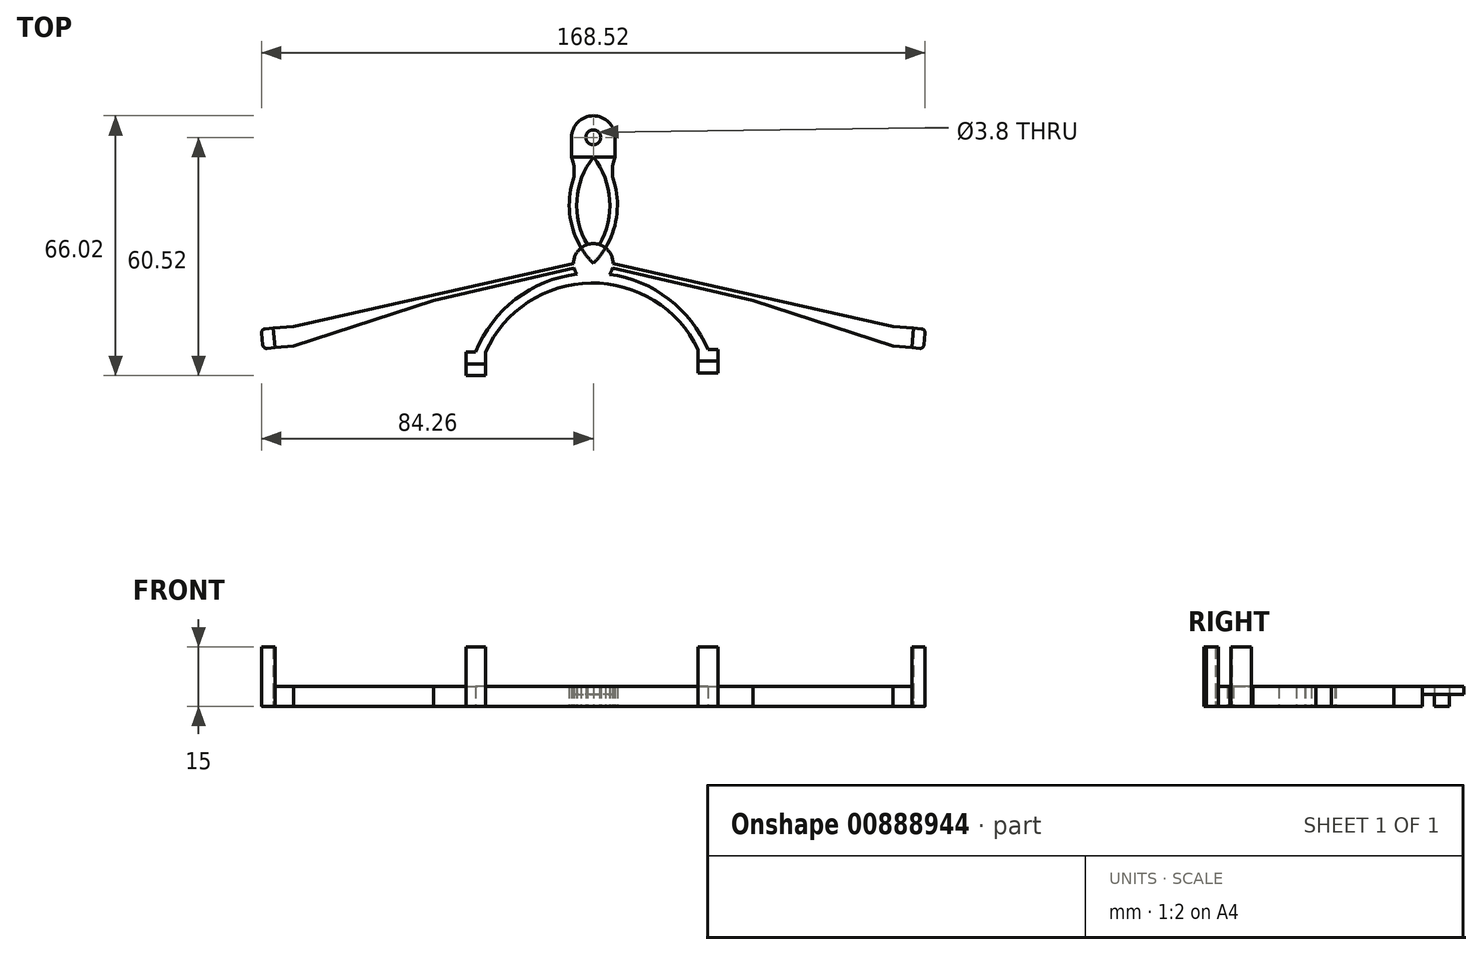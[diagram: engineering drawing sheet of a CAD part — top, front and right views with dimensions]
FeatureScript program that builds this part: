
annotation { "Feature Type Name" : "Feature", "Feature Type Description" : "" }
export const myFeature = defineFeature(function(context is Context, id is Id, definition is map)
    precondition{}
    {
        {
            var Q0;
            Q0=qCreatedBy(makeId("Top.planeOp"),FACE);
            var sketch = newSketch(context, id + "F0", { "sketchPlane" : qUnion([Q0])});
            skLineSegment(sketch, "E0.bottom", {"start": v(82.5, 27) * mm, "end": v(-82.5, 27) * mm, "construction": true});
            skLineSegment(sketch, "E0.top", {"start": v(82.5, -27) * mm, "end": v(-82.5, -27) * mm, "construction": true});
            skPoint(sketch, "E0.middle", {"position": v(0, 0) * mm});
            skPoint(sketch, "E1", {"position": v(0, 27) * mm});
            skPoint(sketch, "E2.middle", {"position": v(0, 29.5) * mm});
            skCircle(sketch, "E3", {"center": v(0, 32) * mm, "radius": 1.9 * mm});
            skLineSegment(sketch, "E4.bottom", {"start": v(-5.5, 27) * mm, "end": v(5.5, 27) * mm});
            skLineSegment(sketch, "E4.left", {"start": v(-5.5, 27) * mm, "end": v(-5.5, 32) * mm});
            skLineSegment(sketch, "E4.right", {"start": v(5.5, 27) * mm, "end": v(5.5, 32) * mm});
            skArc(sketch, "E5", {"start": v(5.5, 32) * mm, "mid": v(0, 37.5) * mm, "end": v(-5.5, 32) * mm});
            skCircle(sketch, "E6", {"center": v(0, 0) * mm, "radius": 5 * mm});
            skLineSegment(sketch, "E7", {"start": v(-82.5, 0) * mm, "end": v(82.5, 0) * mm, "construction": true});
            skArc(sketch, "E8", {"start": v(0, 29.5) * mm, "mid": v(-6.1, 14.75) * mm, "end": v(0, 0) * mm});
            skArc(sketch, "E9", {"start": v(0, 0) * mm, "mid": v(6.1, 14.75) * mm, "end": v(0, 29.5) * mm});
            skPoint(sketch, "E10", {"position": v(0, 5) * mm});
            skPoint(sketch, "E11", {"position": v(0, 2.5) * mm});
            skArc(sketch, "E12", {"start": v(0, 2.5) * mm, "mid": v(4.22, 14.75) * mm, "end": v(0, 27) * mm});
            skArc(sketch, "E13", {"start": v(0, 27) * mm, "mid": v(-4.23, 14.75) * mm, "end": v(0, 2.5) * mm});
            skLineSegment(sketch, "E14", {"start": v(-5, 0) * mm, "end": v(0, 0) * mm});
            skLineSegment(sketch, "E15", {"start": v(5, 0) * mm, "end": v(0, 0) * mm});
            skPoint(sketch, "E16", {"position": v(-2.5, 0) * mm});
            skPoint(sketch, "E17", {"position": v(2.5, 0) * mm});
            skArc(sketch, "E18", {"start": v(5.5, 27) * mm, "mid": v(4.84, 23.38) * mm, "end": v(5.5, 19.76) * mm});
            skArc(sketch, "E19", {"start": v(-5.5, 19.76) * mm, "mid": v(-4.87, 23.38) * mm, "end": v(-5.5, 27) * mm});
            skLineSegment(sketch, "E20", {"start": v(-82.5, -27) * mm, "end": v(-82.5, 27) * mm});
            skLineSegment(sketch, "E21", {"start": v(-80.9, -21.44) * mm, "end": v(-81.35, -16.46) * mm});
            skLineSegment(sketch, "E22", {"start": v(-80.9, -21.44) * mm, "end": v(-82.93, -21.62) * mm});
            skLineSegment(sketch, "E23", {"start": v(-81.35, -16.46) * mm, "end": v(-83.37, -16.64) * mm});
            skLineSegment(sketch, "E24", {"start": v(-83.98, -20.74) * mm, "end": v(-84.25, -17.7) * mm});
            skPoint(sketch, "E25.visualSharp", {"position": v(-84.34, -16.73) * mm});
            skArc(sketch, "E25.filletArc", {"start": v(-83.37, -16.64) * mm, "mid": v(-84.03, -16.99) * mm, "end": v(-84.25, -17.7) * mm});
            skPoint(sketch, "E26.visualSharp", {"position": v(-83.9, -21.71) * mm});
            skArc(sketch, "E26.filletArc", {"start": v(-83.98, -20.74) * mm, "mid": v(-83.64, -21.4) * mm, "end": v(-82.93, -21.62) * mm});
            skPoint(sketch, "E27", {"position": v(-81.13, -18.95) * mm});
            skLineSegment(sketch, "E28", {"start": v(82.5, -27) * mm, "end": v(82.5, 0) * mm});
            skLineSegment(sketch, "E29", {"start": v(-80.9, -21.44) * mm, "end": v(-80.9, -27) * mm});
            skLineSegment(sketch, "E30", {"start": v(80.9, -21.44) * mm, "end": v(81.35, -16.46) * mm});
            skLineSegment(sketch, "E31", {"start": v(81.35, -16.46) * mm, "end": v(83.37, -16.64) * mm});
            skLineSegment(sketch, "E32", {"start": v(84.25, -17.7) * mm, "end": v(83.98, -20.74) * mm});
            skLineSegment(sketch, "E33", {"start": v(82.93, -21.62) * mm, "end": v(80.9, -21.44) * mm});
            skPoint(sketch, "E34.visualSharp", {"position": v(84.34, -16.73) * mm});
            skArc(sketch, "E34.filletArc", {"start": v(84.25, -17.7) * mm, "mid": v(84.03, -16.99) * mm, "end": v(83.37, -16.64) * mm});
            skPoint(sketch, "E35.visualSharp", {"position": v(83.9, -21.71) * mm});
            skArc(sketch, "E35.filletArc", {"start": v(82.93, -21.62) * mm, "mid": v(83.64, -21.4) * mm, "end": v(83.98, -20.74) * mm});
            skPoint(sketch, "E36", {"position": v(81.13, -18.95) * mm});
            skLineSegment(sketch, "E37", {"start": v(-81.35, -16.46) * mm, "end": v(-76.11, -16) * mm});
            skLineSegment(sketch, "E38", {"start": v(-80.9, -21.44) * mm, "end": v(-76.11, -21.02) * mm});
            skLineSegment(sketch, "E39", {"start": v(-76.11, -21.02) * mm, "end": v(-76.11, -16) * mm});
            skLineSegment(sketch, "E40", {"start": v(81.35, -16.46) * mm, "end": v(76.11, -16) * mm});
            skLineSegment(sketch, "E41", {"start": v(80.9, -21.44) * mm, "end": v(76.11, -21.02) * mm});
            skLineSegment(sketch, "E42", {"start": v(76.11, -21.02) * mm, "end": v(76.11, -16) * mm});
            skLineSegment(sketch, "E43", {"start": v(81.13, -18.95) * mm, "end": v(0, 0) * mm});
            skLineSegment(sketch, "E44", {"start": v(-81.13, -18.95) * mm, "end": v(0, 0) * mm});
            skLineSegment(sketch, "E45", {"start": v(-76.11, -16) * mm, "end": v(-5, 0) * mm});
            skPoint(sketch, "E46", {"position": v(-40.56, -9.48) * mm});
            skLineSegment(sketch, "E47", {"start": v(-76.11, -21.02) * mm, "end": v(-40.56, -9.48) * mm});
            skLineSegment(sketch, "E48", {"start": v(5, 0) * mm, "end": v(76.11, -16) * mm});
            skPoint(sketch, "E49", {"position": v(40.56, -9.48) * mm});
            skLineSegment(sketch, "E50", {"start": v(76.11, -21.02) * mm, "end": v(40.56, -9.48) * mm});
            skLineSegment(sketch, "E51", {"start": v(-29.88, -25.53) * mm, "end": v(-32.38, -25.52) * mm});
            skLineSegment(sketch, "E52", {"start": v(-29.88, -25.53) * mm, "end": v(-27.38, -25.53) * mm});
            skLineSegment(sketch, "E53.bottom", {"start": v(-32.38, -25.52) * mm, "end": v(-27.38, -25.52) * mm});
            skLineSegment(sketch, "E53.top", {"start": v(-32.38, -28.52) * mm, "end": v(-27.38, -28.52) * mm});
            skLineSegment(sketch, "E53.left", {"start": v(-32.38, -25.52) * mm, "end": v(-32.38, -28.52) * mm});
            skLineSegment(sketch, "E53.right", {"start": v(-27.38, -25.52) * mm, "end": v(-27.38, -28.52) * mm});
            skLineSegment(sketch, "E54.top", {"start": v(-32.38, -22.52) * mm, "end": v(-27.38, -22.52) * mm});
            skLineSegment(sketch, "E54.left", {"start": v(-32.38, -25.52) * mm, "end": v(-32.38, -22.52) * mm});
            skLineSegment(sketch, "E54.right", {"start": v(-27.38, -25.52) * mm, "end": v(-27.38, -22.52) * mm});
            skLineSegment(sketch, "E55.bottom", {"start": v(26.62, -24.88) * mm, "end": v(31.62, -24.88) * mm});
            skLineSegment(sketch, "E55.top", {"start": v(26.62, -21.88) * mm, "end": v(31.62, -21.88) * mm});
            skLineSegment(sketch, "E55.left", {"start": v(26.62, -24.88) * mm, "end": v(26.62, -21.88) * mm});
            skLineSegment(sketch, "E55.right", {"start": v(31.62, -24.88) * mm, "end": v(31.62, -21.88) * mm});
            skLineSegment(sketch, "E56.bottom", {"start": v(31.62, -24.88) * mm, "end": v(26.62, -24.88) * mm});
            skLineSegment(sketch, "E56.top", {"start": v(31.62, -27.88) * mm, "end": v(26.62, -27.88) * mm});
            skLineSegment(sketch, "E56.left", {"start": v(31.62, -24.88) * mm, "end": v(31.62, -27.88) * mm});
            skLineSegment(sketch, "E56.right", {"start": v(26.62, -24.88) * mm, "end": v(26.62, -27.88) * mm});
            skLineSegment(sketch, "E57", {"start": v(0, 0) * mm, "end": v(0, -5) * mm});
            skLineSegment(sketch, "E58", {"start": v(29.12, -24.88) * mm, "end": v(29.12, -21.88) * mm});
            skLineSegment(sketch, "E59", {"start": v(-29.88, -25.53) * mm, "end": v(-29.88, -22.52) * mm});
            skPoint(sketch, "E60", {"position": v(0, -2.5) * mm});
            skArc(sketch, "E61", {"start": v(29.12, -21.88) * mm, "mid": v(-0.6, -2.5) * mm, "end": v(-29.88, -22.52) * mm});
            skArc(sketch, "E62", {"start": v(26.62, -21.88) * mm, "mid": v(-0.59, -5) * mm, "end": v(-27.38, -22.52) * mm});
            skSolve(sketch);
        }
        {
            var Q0;
            Q0=makeQuery(id+"F0.imprint","IMPRINT",FACE,{"disambiguationData":[TD([[makeQuery(id+"F0.imprint","IMPRINT",EDGE,{"derivedFrom":sQuery(id+"F0.wireOp",EDGE,"E24")}),-1.0]])]});
            var Q1;
            {var subQ0=sQuery(id+"F0.wireOp",EDGE,"E22");var subQ3=sQuery(id+"F0.wireOp",EDGE,"E20");var subQ4=makeQuery(id+"F0.imprint","INTERSECT",VERTEX,{"derivedFrom":[subQ3,subQ0]});Q1=makeQuery(id+"F0.imprint","IMPRINT",FACE,{"disambiguationData":[TD([[makeQuery(id+"F0.imprint","IMPRINT",EDGE,{"disambiguationData":[TD([[subQ4,-1.0]])],"derivedFrom":subQ3}),-1.0]])]});}
            var Q2;
            Q2=makeQuery(id+"F0.imprint","IMPRINT",FACE,{"disambiguationData":[TD([[makeQuery(id+"F0.imprint","IMPRINT",EDGE,{"derivedFrom":sQuery(id+"F0.wireOp",EDGE,"E32")}),-1.0]])]});
            var Q3;
            {var subQ0=sQuery(id+"F0.wireOp",EDGE,"E31");var subQ3=sQuery(id+"F0.wireOp",EDGE,"E28");var subQ4=makeQuery(id+"F0.imprint","INTERSECT",VERTEX,{"derivedFrom":[subQ3,subQ0]});Q3=makeQuery(id+"F0.imprint","IMPRINT",FACE,{"disambiguationData":[TD([[makeQuery(id+"F0.imprint","IMPRINT",EDGE,{"disambiguationData":[TD([[subQ4,1.0]])],"derivedFrom":subQ3}),1.0]])]});}
            var Q4;
            Q4=makeQuery(id+"F0.imprint","IMPRINT",FACE,{"disambiguationData":[TD([[makeQuery(id+"F0.imprint","IMPRINT",EDGE,{"derivedFrom":sQuery(id+"F0.wireOp",EDGE,"E56.top")}),-1.0]])]});
            var Q5;
            Q5=makeQuery(id+"F0.imprint","IMPRINT",FACE,{"disambiguationData":[TD([[makeQuery(id+"F0.imprint","IMPRINT",EDGE,{"derivedFrom":sQuery(id+"F0.wireOp",EDGE,"E51")}),1.0]])]});
            extrude(context, id + "F1", {"entities" : qUnion([Q0, Q1, Q2, Q3, Q4, Q5]), "depth" : 15 * mm, "offsetDistance" : 25 * mm});
        }
        {
            var Q0;
            {var subQ0=sQuery(id+"F0.wireOp",EDGE,"E18");var subQ3=sQuery(id+"F0.wireOp",EDGE,"E9");var subQ5=makeQuery(id+"F0.imprint","INTERSECT",VERTEX,{"disambiguationData":[OD(1.0)],"derivedFrom":[subQ3,subQ0]});Q0=makeQuery(id+"F0.imprint","IMPRINT",FACE,{"disambiguationData":[TD([[makeQuery(id+"F0.imprint","IMPRINT",EDGE,{"disambiguationData":[TD([[subQ5,-1.0]])],"derivedFrom":subQ3}),-1.0]])]});}
            var Q1;
            {var subQ1=sQuery(id+"F0.wireOp",EDGE,"E9");var subQ3=sQuery(id+"F0.wireOp",EDGE,"E6");var subQ4=makeQuery(id+"F0.imprint","INTERSECT",VERTEX,{"derivedFrom":[subQ3,subQ1]});Q1=makeQuery(id+"F0.imprint","IMPRINT",FACE,{"disambiguationData":[TD([[makeQuery(id+"F0.imprint","IMPRINT",EDGE,{"disambiguationData":[TD([[subQ4,-1.0]])],"derivedFrom":subQ3}),-1.0]])]});}
            var Q2;
            {var subQ1=sQuery(id+"F0.wireOp",EDGE,"E8");var subQ3=sQuery(id+"F0.wireOp",EDGE,"E6");var subQ4=makeQuery(id+"F0.imprint","INTERSECT",VERTEX,{"derivedFrom":[subQ3,subQ1]});Q2=makeQuery(id+"F0.imprint","IMPRINT",FACE,{"disambiguationData":[TD([[makeQuery(id+"F0.imprint","IMPRINT",EDGE,{"disambiguationData":[TD([[subQ4,1.0]])],"derivedFrom":subQ3}),-1.0]])]});}
            var Q3;
            {var subQ0=sQuery(id+"F0.wireOp",EDGE,"E19");var subQ3=sQuery(id+"F0.wireOp",EDGE,"E8");var subQ5=makeQuery(id+"F0.imprint","INTERSECT",VERTEX,{"disambiguationData":[OD(1.0)],"derivedFrom":[subQ3,subQ0]});Q3=makeQuery(id+"F0.imprint","IMPRINT",FACE,{"disambiguationData":[TD([[makeQuery(id+"F0.imprint","IMPRINT",EDGE,{"disambiguationData":[TD([[subQ5,1.0]])],"derivedFrom":subQ3}),-1.0]])]});}
            var Q4;
            {var subQ0=sQuery(id+"F0.wireOp",EDGE,"E15");Q4=makeQuery(id+"F0.imprint","IMPRINT",FACE,{"disambiguationData":[TD([[makeQuery(id+"F0.imprint","IMPRINT",EDGE,{"derivedFrom":subQ0}),-1.0]])]});}
            var Q5;
            {var subQ0=sQuery(id+"F0.wireOp",EDGE,"E14");Q5=makeQuery(id+"F0.imprint","IMPRINT",FACE,{"disambiguationData":[TD([[makeQuery(id+"F0.imprint","IMPRINT",EDGE,{"derivedFrom":subQ0}),1.0]])]});}
            var Q6;
            {var subQ0=sQuery(id+"F0.wireOp",EDGE,"E14");Q6=makeQuery(id+"F0.imprint","IMPRINT",FACE,{"disambiguationData":[TD([[makeQuery(id+"F0.imprint","IMPRINT",EDGE,{"derivedFrom":subQ0}),-1.0]])]});}
            var Q7;
            {var subQ0=sQuery(id+"F0.wireOp",EDGE,"E44");var subQ1=sQuery(id+"F0.wireOp",EDGE,"E6");var subQ2=makeQuery(id+"F0.imprint","INTERSECT",VERTEX,{"derivedFrom":[subQ1,subQ0]});Q7=makeQuery(id+"F0.imprint","IMPRINT",FACE,{"disambiguationData":[TD([[makeQuery(id+"F0.imprint","IMPRINT",EDGE,{"disambiguationData":[TD([[subQ2,-1.0]])],"derivedFrom":subQ1}),1.0]])]});}
            var Q8;
            {var subQ0=sQuery(id+"F0.wireOp",EDGE,"E62");var subQ1=sQuery(id+"F0.wireOp",EDGE,"E6");var subQ2=makeQuery(id+"F0.imprint","INTERSECT",VERTEX,{"derivedFrom":[subQ1,subQ0]});Q8=makeQuery(id+"F0.imprint","IMPRINT",FACE,{"disambiguationData":[TD([[makeQuery(id+"F0.imprint","IMPRINT",EDGE,{"disambiguationData":[TD([[subQ2,1.0]])],"derivedFrom":subQ1}),1.0]])]});}
            var Q9;
            {var subQ0=sQuery(id+"F0.wireOp",EDGE,"E61");var subQ1=sQuery(id+"F0.wireOp",EDGE,"E6");var subQ2=makeQuery(id+"F0.imprint","INTERSECT",VERTEX,{"disambiguationData":[OD(1.0)],"derivedFrom":[subQ1,subQ0]});Q9=makeQuery(id+"F0.imprint","IMPRINT",FACE,{"disambiguationData":[TD([[makeQuery(id+"F0.imprint","IMPRINT",EDGE,{"disambiguationData":[TD([[subQ2,-1.0]])],"derivedFrom":subQ1}),1.0]])]});}
            var Q10;
            {var subQ0=sQuery(id+"F0.wireOp",EDGE,"E15");Q10=makeQuery(id+"F0.imprint","IMPRINT",FACE,{"disambiguationData":[TD([[makeQuery(id+"F0.imprint","IMPRINT",EDGE,{"derivedFrom":subQ0}),1.0]])]});}
            var Q11;
            {var subQ1=sQuery(id+"F0.wireOp",EDGE,"E6");var subQ3=sQuery(id+"F0.wireOp",EDGE,"E61");var subQ4=makeQuery(id+"F0.imprint","INTERSECT",VERTEX,{"disambiguationData":[OD(1.0)],"derivedFrom":[subQ1,subQ3]});Q11=makeQuery(id+"F0.imprint","IMPRINT",FACE,{"disambiguationData":[TD([[makeQuery(id+"F0.imprint","IMPRINT",EDGE,{"disambiguationData":[TD([[subQ4,-1.0]])],"derivedFrom":subQ3}),1.0]])]});}
            var Q12;
            {var subQ1=sQuery(id+"F0.wireOp",EDGE,"E6");var subQ3=sQuery(id+"F0.wireOp",EDGE,"E61");var subQ4=makeQuery(id+"F0.imprint","INTERSECT",VERTEX,{"disambiguationData":[OD(1.0)],"derivedFrom":[subQ1,subQ3]});Q12=makeQuery(id+"F0.imprint","IMPRINT",FACE,{"disambiguationData":[TD([[makeQuery(id+"F0.imprint","IMPRINT",EDGE,{"disambiguationData":[TD([[subQ4,1.0]])],"derivedFrom":subQ1}),-1.0]])]});}
            var Q13;
            {var subQ0=sQuery(id+"F0.wireOp",EDGE,"E62");var subQ1=sQuery(id+"F0.wireOp",EDGE,"E6");var subQ2=makeQuery(id+"F0.imprint","INTERSECT",VERTEX,{"derivedFrom":[subQ1,subQ0]});Q13=makeQuery(id+"F0.imprint","IMPRINT",FACE,{"disambiguationData":[TD([[makeQuery(id+"F0.imprint","IMPRINT",EDGE,{"disambiguationData":[TD([[subQ2,1.0]])],"derivedFrom":subQ1}),-1.0]])]});}
            var Q14;
            {var subQ4=sQuery(id+"F0.wireOp",EDGE,"E45");Q14=makeQuery(id+"F0.imprint","IMPRINT",FACE,{"disambiguationData":[TD([[makeQuery(id+"F0.imprint","IMPRINT",EDGE,{"derivedFrom":subQ4}),-1.0]])]});}
            var Q15;
            {var subQ4=sQuery(id+"F0.wireOp",EDGE,"E48");Q15=makeQuery(id+"F0.imprint","IMPRINT",FACE,{"disambiguationData":[TD([[makeQuery(id+"F0.imprint","IMPRINT",EDGE,{"derivedFrom":subQ4}),-1.0]])]});}
            var Q16;
            {var subQ0=sQuery(id+"F0.wireOp",EDGE,"E50");Q16=makeQuery(id+"F0.imprint","IMPRINT",FACE,{"disambiguationData":[TD([[makeQuery(id+"F0.imprint","IMPRINT",EDGE,{"derivedFrom":subQ0}),-1.0]])]});}
            var Q17;
            {var subQ0=sQuery(id+"F0.wireOp",EDGE,"E40");Q17=makeQuery(id+"F0.imprint","IMPRINT",FACE,{"disambiguationData":[TD([[makeQuery(id+"F0.imprint","IMPRINT",EDGE,{"derivedFrom":subQ0}),1.0]])]});}
            var Q18;
            {var subQ0=sQuery(id+"F0.wireOp",EDGE,"E41");Q18=makeQuery(id+"F0.imprint","IMPRINT",FACE,{"disambiguationData":[TD([[makeQuery(id+"F0.imprint","IMPRINT",EDGE,{"derivedFrom":subQ0}),-1.0]])]});}
            var Q19;
            {var subQ0=sQuery(id+"F0.wireOp",EDGE,"E47");Q19=makeQuery(id+"F0.imprint","IMPRINT",FACE,{"disambiguationData":[TD([[makeQuery(id+"F0.imprint","IMPRINT",EDGE,{"derivedFrom":subQ0}),1.0]])]});}
            var Q20;
            {var subQ0=sQuery(id+"F0.wireOp",EDGE,"E38");Q20=makeQuery(id+"F0.imprint","IMPRINT",FACE,{"disambiguationData":[TD([[makeQuery(id+"F0.imprint","IMPRINT",EDGE,{"derivedFrom":subQ0}),1.0]])]});}
            var Q21;
            {var subQ0=sQuery(id+"F0.wireOp",EDGE,"E37");Q21=makeQuery(id+"F0.imprint","IMPRINT",FACE,{"disambiguationData":[TD([[makeQuery(id+"F0.imprint","IMPRINT",EDGE,{"derivedFrom":subQ0}),-1.0]])]});}
            var Q22;
            {var subQ0=sQuery(id+"F0.wireOp",EDGE,"E54.left");Q22=makeQuery(id+"F0.imprint","IMPRINT",FACE,{"disambiguationData":[TD([[makeQuery(id+"F0.imprint","IMPRINT",EDGE,{"derivedFrom":subQ0}),-1.0]])]});}
            var Q23;
            {var subQ0=sQuery(id+"F0.wireOp",EDGE,"E54.right");Q23=makeQuery(id+"F0.imprint","IMPRINT",FACE,{"disambiguationData":[TD([[makeQuery(id+"F0.imprint","IMPRINT",EDGE,{"derivedFrom":subQ0}),1.0]])]});}
            var Q24;
            {var subQ0=sQuery(id+"F0.wireOp",EDGE,"E55.left");Q24=makeQuery(id+"F0.imprint","IMPRINT",FACE,{"disambiguationData":[TD([[makeQuery(id+"F0.imprint","IMPRINT",EDGE,{"derivedFrom":subQ0}),-1.0]])]});}
            var Q25;
            {var subQ0=sQuery(id+"F0.wireOp",EDGE,"E55.right");Q25=makeQuery(id+"F0.imprint","IMPRINT",FACE,{"disambiguationData":[TD([[makeQuery(id+"F0.imprint","IMPRINT",EDGE,{"derivedFrom":subQ0}),1.0]])]});}
            extrude(context, id + "F2", {"entities" : qUnion([Q0, Q1, Q2, Q3, Q4, Q5, Q6, Q7, Q8, Q9, Q10, Q11, Q12, Q13, Q14, Q15, Q16, Q17, Q18, Q19, Q20, Q21, Q22, Q23, Q24, Q25]), "depth" : 5 * mm, "offsetDistance" : 25 * mm});
        }
        {
            var Q0;
            {var subQ0=sQuery(id+"F0.wireOp",EDGE,"E12");var subQ1=sQuery(id+"F0.wireOp",EDGE,"E6");var subQ2=makeQuery(id+"F0.imprint","INTERSECT",VERTEX,{"derivedFrom":[subQ1,subQ0]});Q0=makeQuery(id+"F0.imprint","IMPRINT",FACE,{"disambiguationData":[TD([[makeQuery(id+"F0.imprint","IMPRINT",EDGE,{"disambiguationData":[TD([[subQ2,-1.0]])],"derivedFrom":subQ1}),1.0]])]});}
            var Q1;
            {var subQ0=sQuery(id+"F0.wireOp",EDGE,"E9");var subQ3=sQuery(id+"F0.wireOp",EDGE,"E6");var subQ4=makeQuery(id+"F0.imprint","INTERSECT",VERTEX,{"derivedFrom":[subQ3,subQ0]});Q1=makeQuery(id+"F0.imprint","IMPRINT",FACE,{"disambiguationData":[TD([[makeQuery(id+"F0.imprint","IMPRINT",EDGE,{"disambiguationData":[TD([[subQ4,-1.0]])],"derivedFrom":subQ3}),1.0]])]});}
            extrude(context, id + "F3", {"entities" : qUnion([Q0, Q1]), "depth" : 5 * mm, "offsetDistance" : 25 * mm});
        }
        {
            var Q0;
            Q0=makeQuery(id+"F0.imprint","IMPRINT",FACE,{"disambiguationData":[TD([[makeQuery(id+"F0.imprint","IMPRINT",EDGE,{"derivedFrom":sQuery(id+"F0.wireOp",EDGE,"E3")}),1.0]])]});
            extrude(context, id + "F4", {"entities" : qUnion([Q0]), "depth" : 5 * mm, "offsetDistance" : 25 * mm});
        }
        {
            var Q0;
            Q0=makeQuery(id+"F0.imprint","IMPRINT",FACE,{"disambiguationData":[TD([[makeQuery(id+"F0.imprint","IMPRINT",EDGE,{"derivedFrom":sQuery(id+"F0.wireOp",EDGE,"E3")}),-1.0]])]});
            var Q1;
            {var subQ2=sQuery(id+"F0.wireOp",EDGE,"E8");var subQ4=sQuery(id+"F0.wireOp",EDGE,"E9");var subQ6=makeQuery(id+"F0.imprint","INTERSECT",VERTEX,{"derivedFrom":[subQ2,subQ4]});Q1=makeQuery(id+"F0.imprint","IMPRINT",FACE,{"disambiguationData":[TD([[makeQuery(id+"F0.imprint","IMPRINT",EDGE,{"disambiguationData":[TD([[subQ6,-1.0]])],"derivedFrom":subQ2}),1.0]])]});}
            extrude(context, id + "F5", {"entities" : qUnion([Q0, Q1]), "depth" : 5 * mm, "offsetDistance" : 25 * mm});
        }
        {
            var Q0;
            Q0=makeQuery(id+"F0.imprint","IMPRINT",FACE,{"disambiguationData":[TD([[makeQuery(id+"F0.imprint","IMPRINT",EDGE,{"derivedFrom":sQuery(id+"F0.wireOp",EDGE,"E3")}),-1.0]])]});
            var Q1;
            {var subQ2=sQuery(id+"F0.wireOp",EDGE,"E8");var subQ4=sQuery(id+"F0.wireOp",EDGE,"E9");var subQ6=makeQuery(id+"F0.imprint","INTERSECT",VERTEX,{"derivedFrom":[subQ2,subQ4]});Q1=makeQuery(id+"F0.imprint","IMPRINT",FACE,{"disambiguationData":[TD([[makeQuery(id+"F0.imprint","IMPRINT",EDGE,{"disambiguationData":[TD([[subQ6,-1.0]])],"derivedFrom":subQ2}),1.0]])]});}
            extrude(context, id + "F6", {"entities" : qUnion([Q0, Q1]), "operationType" : NewBodyOperationType.REMOVE, "depth" : 3 * mm, "offsetDistance" : 25 * mm});
        }
    });
